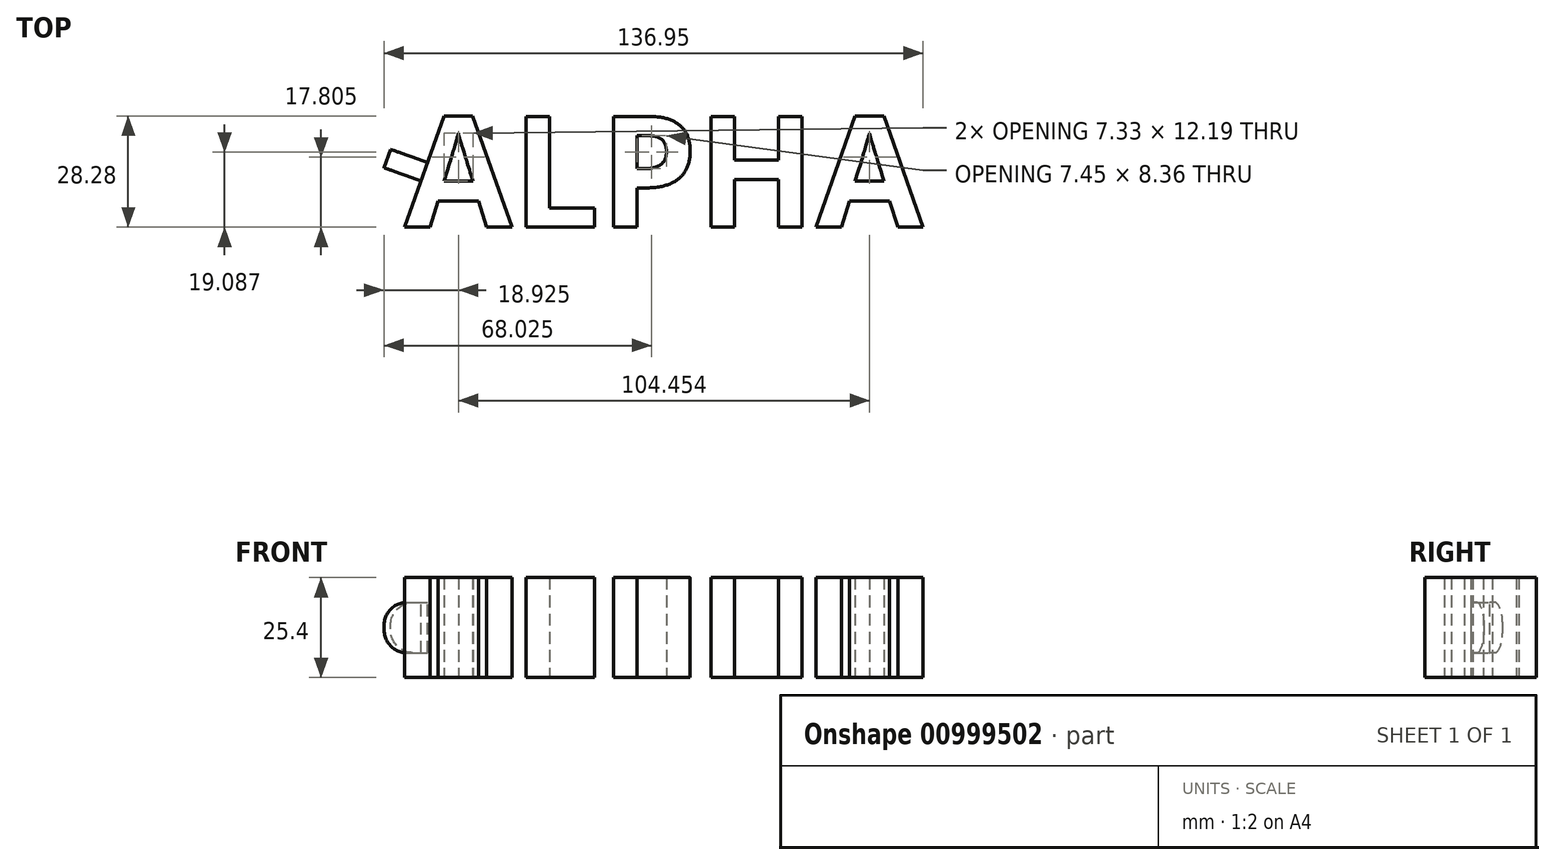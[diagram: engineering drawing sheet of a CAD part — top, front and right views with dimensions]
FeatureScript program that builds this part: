
annotation { "Feature Type Name" : "Feature", "Feature Type Description" : "" }
export const myFeature = defineFeature(function(context is Context, id is Id, definition is map)
    precondition{}
    {
        {
            var Q0;
            Q0=qCreatedBy(makeId("Top.planeOp"),FACE);
            var sketch = newSketch(context, id + "F0", { "sketchPlane" : qUnion([Q0])});
            skText(sketch, "E0", { "text": "ALPHA", "fontName": "OpenSans-Bold.ttf"});
            const initialGuessF0  = {"E0": [0, 0, 1, 0, 0.0284]};
            skSetInitialGuess(sketch, initialGuessF0);
            skSolve(sketch);
        }
        {
            var Q0;
            Q0=makeQuery(id+"F0.imprint","IMPRINT",FACE,{"disambiguationData":[TD([[makeQuery(id+"F0.imprint","IMPRINT",EDGE,{"derivedFrom":sQuery(id+"F0.wireOp",EDGE,"E0.sketch_text.stroke-0")}),-1.0]])]});
            var Q1;
            Q1=makeQuery(id+"F0.imprint","IMPRINT",FACE,{"disambiguationData":[TD([[makeQuery(id+"F0.imprint","IMPRINT",EDGE,{"derivedFrom":sQuery(id+"F0.wireOp",EDGE,"E0.sketch_text.stroke-12")}),-1.0]])]});
            var Q2;
            Q2=makeQuery(id+"F0.imprint","IMPRINT",FACE,{"disambiguationData":[TD([[makeQuery(id+"F0.imprint","IMPRINT",EDGE,{"derivedFrom":sQuery(id+"F0.wireOp",EDGE,"E0.sketch_text.stroke-18")}),-1.0]])]});
            var Q3;
            Q3=makeQuery(id+"F0.imprint","IMPRINT",FACE,{"disambiguationData":[TD([[makeQuery(id+"F0.imprint","IMPRINT",EDGE,{"derivedFrom":sQuery(id+"F0.wireOp",EDGE,"E0.sketch_text.stroke-34")}),-1.0]])]});
            var Q4;
            Q4=makeQuery(id+"F0.imprint","IMPRINT",FACE,{"disambiguationData":[TD([[makeQuery(id+"F0.imprint","IMPRINT",EDGE,{"derivedFrom":sQuery(id+"F0.wireOp",EDGE,"E0.sketch_text.stroke-46")}),-1.0]])]});
            extrude(context, id + "F1", {"entities" : qUnion([Q0, Q1, Q2, Q3, Q4]), "depth" : 25.4 * mm, "offsetDistance" : 25.4 * mm});
        }
        {
            var Q0;
            Q0=makeQuery(id+"F1.opExtrude","SWEPT_FACE",FACE,{"disambiguationData":[OSD([sQuery(id+"F0.wireOp",EDGE,"E0.sketch_text.stroke-4")])]});
            var sketch = newSketch(context, id + "F2", { "sketchPlane" : qUnion([Q0])});
            skLineSegment(sketch, "E1", {"start": v(-29.98, 25.4) * mm, "end": v(0, 0) * mm, "construction": true});
            skLineSegment(sketch, "E2", {"start": v(0, 0) * mm, "end": v(-29.98, 0) * mm});
            skLineSegment(sketch, "E3", {"start": v(-29.98, 0) * mm, "end": v(0, 25.4) * mm, "construction": true});
            skLineSegment(sketch, "E4.bottom", {"start": v(-12.51, 6.32) * mm, "end": v(-17.47, 6.32) * mm});
            skLineSegment(sketch, "E4.top", {"start": v(-12.51, 19.08) * mm, "end": v(-17.47, 19.08) * mm});
            skLineSegment(sketch, "E4.left", {"start": v(-12.51, 6.32) * mm, "end": v(-12.51, 19.08) * mm});
            skLineSegment(sketch, "E4.right", {"start": v(-17.47, 6.32) * mm, "end": v(-17.47, 19.08) * mm});
            skPoint(sketch, "E4.middle", {"position": v(-15, 12.7) * mm});
            skSolve(sketch);
        }
        {
            var Q0;
            Q0=makeQuery(id+"F2.imprint","IMPRINT",FACE,{"disambiguationData":[TD([[makeQuery(id+"F2.imprint","IMPRINT",EDGE,{"derivedFrom":sQuery(id+"F2.wireOp",EDGE,"E4.bottom")}),-1.0]])]});
            extrude(context, id + "F3", {"entities" : qUnion([Q0]), "operationType" : NewBodyOperationType.ADD, "depth" : 10 * mm, "offsetDistance" : 25.4 * mm});
        }
        {
            var Q0;
            Q0=makeQuery(id+"F3.opExtrude","CAP_EDGE",EDGE,{"disambiguationData":[OSD([sQuery(id+"F2.wireOp",EDGE,"E4.bottom")])],"isStart":false});
            var Q1;
            Q1=makeQuery(id+"F3.opExtrude","CAP_EDGE",EDGE,{"disambiguationData":[OSD([sQuery(id+"F2.wireOp",EDGE,"E4.top")])],"isStart":false});
            fillet(context, id + "F4", {"entities" : qUnion([Q0, Q1]), "radius" : 6 * mm, "tangentPropagation" : true, "allowEdgeOverflow" : false});
        }
    });
